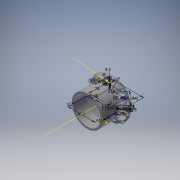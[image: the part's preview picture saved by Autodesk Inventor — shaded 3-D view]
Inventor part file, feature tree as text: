
AUTODESK INVENTOR PART (.ipt)
format: ipt  version: 2016 (Build 200138000, 138)  size: 880,128 bytes
history: native  units: mm
features: sketch x5, extrude x5, other x3, pattern_circular x3, revolve x2, plane x2, chamfer x1
ambient origin geometry x8: Origin, YZ Plane, XZ Plane, XY Plane, X Axis, Y Axis, Z Axis, Center Point
bodies: Solid3 (feature_tree)
feature tree (21):
  sketch  "Sketch1"  dims[d33=20.0mm d56=18.0mm]
  revolve  "Revolution4"  [1 undecoded]
  other  "Work Axis10"
  plane  "Work Plane2"
  sketch  "Sketch5"  dims[d57=30.0deg d58=30.0deg]
  extrude  "Extrusion2"  TaperAngle=30.0deg  [1 undecoded]
  extrude  "Extrusion8"  Depth=15.0mm
  pattern_circular  "Circular Pattern8"  [2 undecoded]
  pattern_circular  "Circular Pattern9"  [2 undecoded]
  chamfer  "Chamfer1"  Distance=2.5mm
  plane  "Work Plane4"
  sketch  "Sketch12"  dims[d59=30.2mm d60=15.0mm]
  extrude  "Extrusion14"  Depth=10.0mm
  extrude  "Extrusion15"  Depth=10.0mm
  extrude  "Extrusion16"  TaperAngle=90.0deg  [1 undecoded]
  pattern_circular  "Circular Pattern11"  [2 undecoded]
  revolve  "Revolution7"  [1 undecoded]
  other  "Work Axis12"
  other  "Work Point7"
  sketch  "Sketch14"  dims[d61=2.0mm]
  sketch  "Sketch15"  dims[d62=2.0mm d74=8.4mm d75=5.8mm d76=2.5mm d77=8.369999mm d78=5.5mm d79=90.0deg d80=2.0mm d81=8.7mm d83=10.0mm d84=0.0mm d88=8.242926mm d95=2.5mm d96=2.7mm d100=6.0mm d103=16.0mm d104=2.8mm d123=10.0mm d124=0.0mm d125=60.0mm d126=360.0deg d128=60.0mm d129=360.0deg d131=19.183807mm d132=0.5mm d133=2.0mm d134=45.0deg d154=12.7mm d155=2.0mm d169=9.2mm d170=1.0mm d171=1.0mm d172=2.5mm d173=0.0mm d174=2.7mm d175=0.0mm d176=1.5mm d177=0.0mm d178=60.0mm d179=360.0deg d181=3.25mm d184=90.0deg d222=40.0mm]
note: 10 required parameter values undecoded (feature->parameter linkage not recoverable at this tier; creation-order binding heuristic only, values carry confidence <= 0.55)